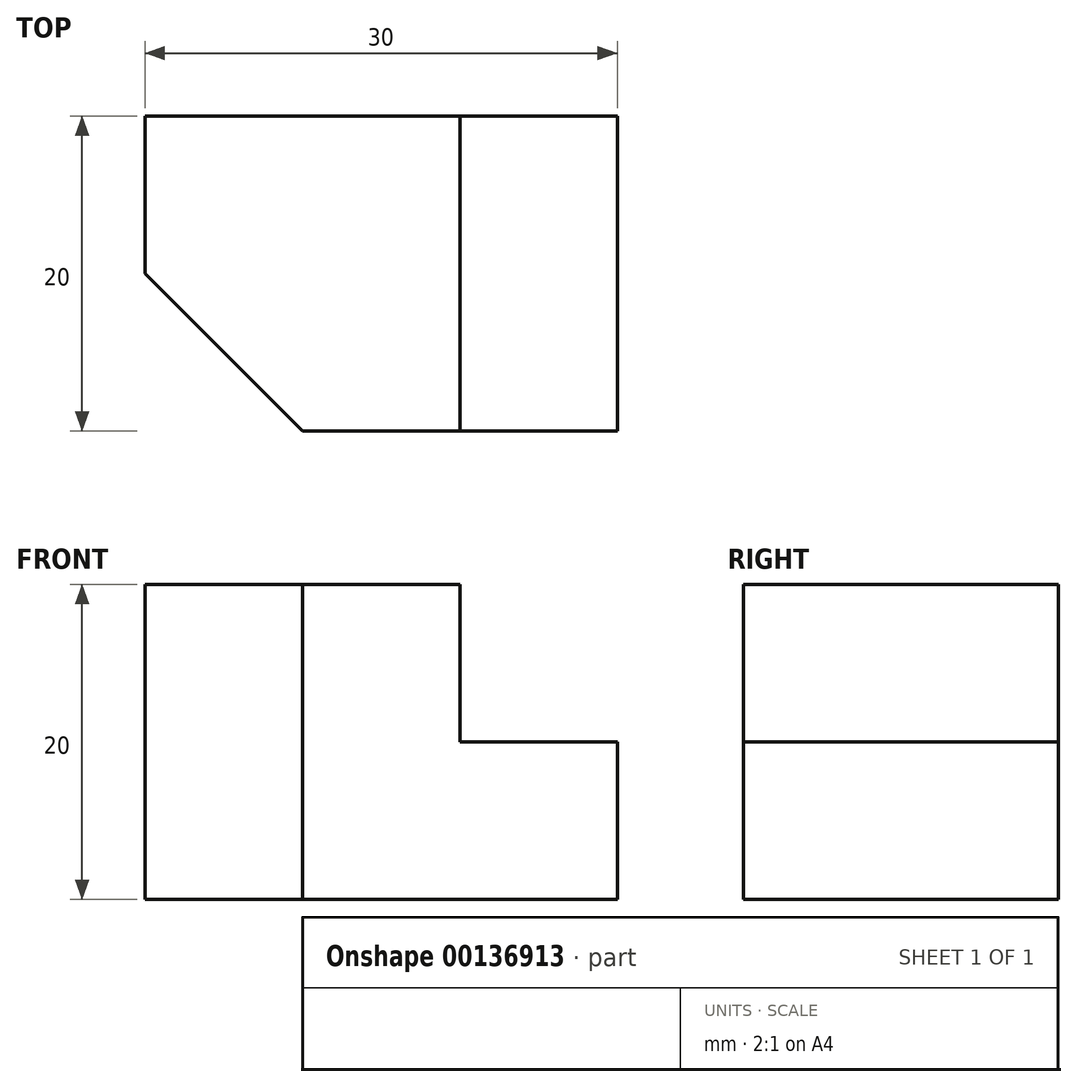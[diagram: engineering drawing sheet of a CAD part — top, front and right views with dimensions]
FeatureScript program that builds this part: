
annotation { "Feature Type Name" : "Feature", "Feature Type Description" : "" }
export const myFeature = defineFeature(function(context is Context, id is Id, definition is map)
    precondition{}
    {
        {
            var Q0;
            Q0=qCreatedBy(makeId("Top.planeOp"),FACE);
            var sketch = newSketch(context, id + "F0", { "sketchPlane" : qUnion([Q0])});
            skLineSegment(sketch, "E0.bottom", {"start": v(10, 0) * mm, "end": v(20, 0) * mm});
            skLineSegment(sketch, "E0.top", {"start": v(0, 20) * mm, "end": v(30, 20) * mm});
            skLineSegment(sketch, "E0.left", {"start": v(0, 10) * mm, "end": v(0, 20) * mm});
            skLineSegment(sketch, "E0.right", {"start": v(30, 0) * mm, "end": v(30, 20) * mm});
            skLineSegment(sketch, "E1", {"start": v(20, 20) * mm, "end": v(20, 0) * mm});
            skLineSegment(sketch, "E2", {"start": v(0, 10) * mm, "end": v(10, 0) * mm});
            skLineSegment(sketch, "E3", {"start": v(20, 0) * mm, "end": v(30, 0) * mm});
            skPoint(sketch, "E4.orphan", {"position": v(0, 0) * mm});
            skSolve(sketch);
        }
        {
            var Q0;
            Q0=makeQuery(id+"F0.imprint","IMPRINT",FACE,{"disambiguationData":[TD([[makeQuery(id+"F0.imprint","IMPRINT",EDGE,{"derivedFrom":sQuery(id+"F0.wireOp",EDGE,"E0.bottom")}),1.0]])]});
            extrude(context, id + "F1", {"entities" : qUnion([Q0]), "depth" : 20 * mm});
        }
        {
            var Q0;
            {var subQ0=sQuery(id+"F0.wireOp",EDGE,"E0.right");Q0=makeQuery(id+"F0.imprint","IMPRINT",FACE,{"disambiguationData":[TD([[makeQuery(id+"F0.imprint","IMPRINT",EDGE,{"derivedFrom":subQ0}),1.0]])]});}
            extrude(context, id + "F2", {"entities" : qUnion([Q0]), "operationType" : NewBodyOperationType.ADD, "depth" : 10 * mm});
        }
    });
